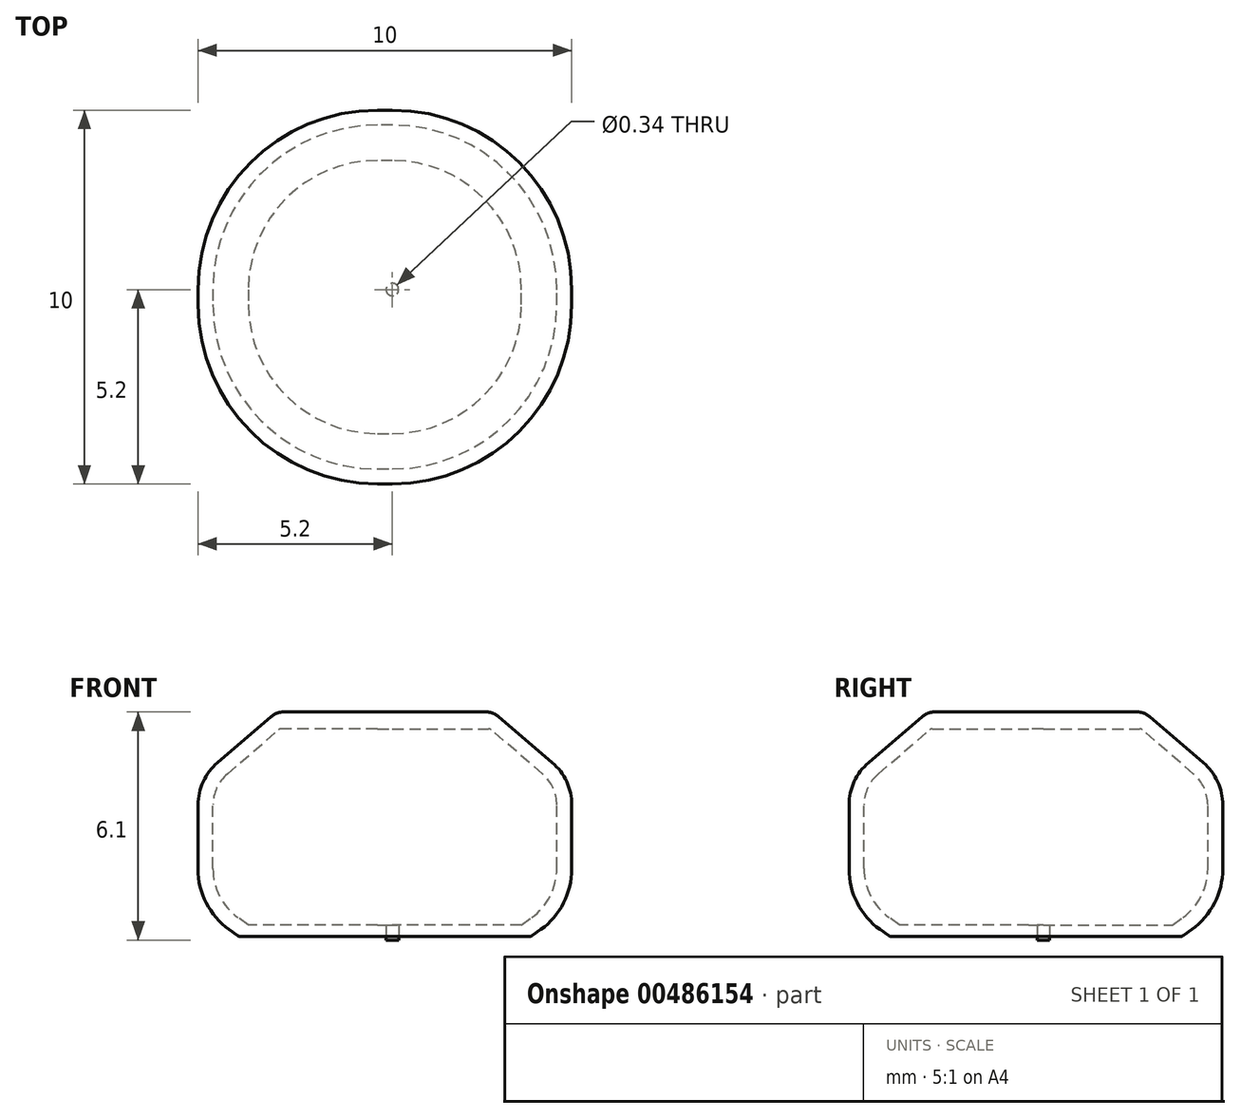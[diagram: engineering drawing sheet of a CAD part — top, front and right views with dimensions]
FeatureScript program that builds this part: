
annotation { "Feature Type Name" : "Feature", "Feature Type Description" : "" }
export const myFeature = defineFeature(function(context is Context, id is Id, definition is map)
    precondition{}
    {
        {
            assignVariable(context, id + "F0", {"name" : "l2", "anyValue" : 0.4});
        }
        {
            assignVariable(context, id + "F1", {"name" : "Scaf", "anyValue" : 0.65});
        }
        {
            var Q0;
            Q0=qCreatedBy(makeId("Front.planeOp"),FACE);
            var sketch = newSketch(context, id + "F2", { "sketchPlane" : qUnion([Q0])});
            skLineSegment(sketch, "E0", {"start": v(0, 0) * mm, "end": v(3.69, 0) * mm});
            skLineSegment(sketch, "E1", {"start": v(4.8, 1.8) * mm, "end": v(4.8, 3.51) * mm});
            skLineSegment(sketch, "E2", {"start": v(2.52, 6) * mm, "end": v(0, 6) * mm});
            skLineSegment(sketch, "E3", {"start": v(3.75, 0.02) * mm, "end": v(3.97, 0.18) * mm});
            skLineSegment(sketch, "E4", {"start": v(4.28, 4.65) * mm, "end": v(2.84, 5.88) * mm});
            skLineSegment(sketch, "E5", {"start": v(0, 0) * mm, "end": v(0, 0.3) * mm});
            skLineSegment(sketch, "E6", {"start": v(0, 0.3) * mm, "end": v(3.45, 0.3) * mm});
            skLineSegment(sketch, "E7", {"start": v(4.4, 1.81) * mm, "end": v(4.4, 3.51) * mm});
            skLineSegment(sketch, "E8", {"start": v(4.02, 4.35) * mm, "end": v(2.64, 5.53) * mm});
            skLineSegment(sketch, "E9", {"start": v(2.57, 5.55) * mm, "end": v(0, 5.55) * mm});
            skLineSegment(sketch, "E10", {"start": v(0, 5.55) * mm, "end": v(0, 6) * mm});
            skLineSegment(sketch, "E11", {"start": v(3.45, 0.3) * mm, "end": v(3.73, 0.5) * mm});
            skPoint(sketch, "E12.visualSharp", {"position": v(4.8, 0.78) * mm});
            skArc(sketch, "E12.filletArc", {"start": v(3.97, 0.18) * mm, "mid": v(4.58, 0.9) * mm, "end": v(4.8, 1.8) * mm});
            skPoint(sketch, "E13.visualSharp", {"position": v(4.8, 4.2) * mm});
            skArc(sketch, "E13.filletArc", {"start": v(4.8, 3.51) * mm, "mid": v(4.66, 4.14) * mm, "end": v(4.28, 4.65) * mm});
            skPoint(sketch, "E14.visualSharp", {"position": v(2.7, 6) * mm});
            skArc(sketch, "E14.filletArc", {"start": v(2.84, 5.88) * mm, "mid": v(2.69, 5.97) * mm, "end": v(2.52, 6) * mm});
            skPoint(sketch, "E15.visualSharp", {"position": v(2.61, 5.55) * mm});
            skArc(sketch, "E15.filletArc", {"start": v(2.64, 5.53) * mm, "mid": v(2.6, 5.54) * mm, "end": v(2.57, 5.55) * mm});
            skPoint(sketch, "E16.visualSharp", {"position": v(4.4, 4.02) * mm});
            skArc(sketch, "E16.filletArc", {"start": v(4.4, 3.51) * mm, "mid": v(4.3, 3.97) * mm, "end": v(4.02, 4.35) * mm});
            skPoint(sketch, "E17.visualSharp", {"position": v(4.4, 0.98) * mm});
            skArc(sketch, "E17.filletArc", {"start": v(3.73, 0.5) * mm, "mid": v(4.22, 1.08) * mm, "end": v(4.4, 1.81) * mm});
            skPoint(sketch, "E18.visualSharp", {"position": v(3.72, 0) * mm});
            skArc(sketch, "E18.filletArc", {"start": v(3.69, 0) * mm, "mid": v(3.72, 0) * mm, "end": v(3.75, 0.02) * mm});
            skSolve(sketch);
        }
        {
            var Q0;
            Q0=makeQuery(id+"F2.imprint","IMPRINT",FACE,{"disambiguationData":[TD([[makeQuery(id+"F2.imprint","IMPRINT",EDGE,{"derivedFrom":sQuery(id+"F2.wireOp",EDGE,"E0")}),1.0]])]});
            extrude(context, id + "F3", {"entities" : qUnion([Q0]), "depth" : (getVariable(context, 'l2')) * mm, "offsetDistance" : 25 * mm});
        }
        {
            var Q0;
            Q0=makeQuery(id+"F3.opExtrude","SWEPT_FACE",FACE,{"disambiguationData":[OSD([sQuery(id+"F2.wireOp",EDGE,"E10")])]});
            var Q1;
            Q1=sQuery(id+"F6.wireOp",EDGE,"E19");
            extrude(context, id + "F4", {"entities" : qUnion([Q0]), "operationType" : NewBodyOperationType.ADD, "surfaceEntities" : qUnion([Q1]), "depth" : (getVariable(context, 'Scaf')) * mm, "offsetDistance" : 25 * mm});
        }
        {
            var Q0;
            Q0=makeQuery(id+"F2.imprint","IMPRINT",FACE,{"disambiguationData":[TD([[makeQuery(id+"F2.imprint","IMPRINT",EDGE,{"derivedFrom":sQuery(id+"F2.wireOp",EDGE,"E0")}),1.0]])]});
            var Q1;
            Q1=sQuery(id+"F2.wireOp",EDGE,"E10");
            revolve(context, id + "F5", {"operationType" : NewBodyOperationType.ADD, "entities" : qUnion([Q0]), "axis" : qUnion([Q1]), "revolveType" : RevolveType.ONE_DIRECTION, "angle" : 90 * degree});
        }
        {
            var Q0;
            Q0=qCreatedBy(makeId("Front.planeOp"),FACE);
            var sketch = newSketch(context, id + "F6", { "sketchPlane" : qUnion([Q0])});
            skLineSegment(sketch, "E19", {"start": v(0, 0) * mm, "end": v(-0.4, 0) * mm});
            skLineSegment(sketch, "E20", {"start": v(-0.4, 0) * mm, "end": v(-0.4, 0.13) * mm});
            skSolve(sketch);
        }
        {
            var Q0;
            Q0=qCreatedBy(makeId("Front.planeOp"),FACE);
            cPlane(context, id + "F7", {"entities" : qUnion([Q0]), "cplaneType" : CPlaneType.OFFSET, "offset" : (getVariable(context, 'l2') / 2) * mm, "width" : 150 * mm, "height" : 150 * mm});
        }
        {
            var Q0;
            Q0=qCreatedBy(id+"F7.planeOp",FACE);
            var sketch = newSketch(context, id + "F8", { "sketchPlane" : qUnion([Q0])});
            skLineSegment(sketch, "E21", {"start": v(0, 0.03) * mm, "end": v(-0.2, 0.03) * mm});
            skLineSegment(sketch, "E22", {"start": v(-0.2, 0.03) * mm, "end": v(-0.2, 0.22) * mm});
            skLineSegment(sketch, "E23", {"start": v(0, 0.03) * mm, "end": v(0, 0.08) * mm});
            skLineSegment(sketch, "E24", {"start": v(0, 0.03) * mm, "end": v(0, 0.14) * mm});
            skPoint(sketch, "E24.endSnap0", {"position": v(0, 0.05) * mm});
            skSolve(sketch);
        }
        {
            var Q0;
            Q0=makeQuery(id+"F3.opExtrude","SWEPT_BODY",BODY,{"disambiguationData":[OSD([sQuery(id+"F2.wireOp",EDGE,"E0"),sQuery(id+"F2.wireOp",EDGE,"E1"),sQuery(id+"F2.wireOp",EDGE,"E2"),sQuery(id+"F2.wireOp",EDGE,"E3"),sQuery(id+"F2.wireOp",EDGE,"E4"),sQuery(id+"F2.wireOp",EDGE,"E5"),sQuery(id+"F2.wireOp",EDGE,"E6"),sQuery(id+"F2.wireOp",EDGE,"E7"),sQuery(id+"F2.wireOp",EDGE,"E8"),sQuery(id+"F2.wireOp",EDGE,"E9"),sQuery(id+"F2.wireOp",EDGE,"E10"),sQuery(id+"F2.wireOp",EDGE,"E11"),sQuery(id+"F2.wireOp",EDGE,"E12.filletArc"),sQuery(id+"F2.wireOp",EDGE,"E13.filletArc"),sQuery(id+"F2.wireOp",EDGE,"E14.filletArc"),sQuery(id+"F2.wireOp",EDGE,"E15.filletArc"),sQuery(id+"F2.wireOp",EDGE,"E16.filletArc"),sQuery(id+"F2.wireOp",EDGE,"E17.filletArc"),sQuery(id+"F2.wireOp",EDGE,"E18.filletArc")])]});
            var Q1;
            Q1=sQuery(id+"F8.wireOp",EDGE,"E22");
            transform(context, id + "F9", {"entities" : qUnion([Q0]), "transformType" : TransformType.ROTATION, "transformAxis" : qUnion([Q1]), "angle" : 90 * degree, "oppositeDirection" : true, "makeCopy" : true});
        }
        {
            var Q0;
            Q0=makeQuery(id+"F3.opExtrude","SWEPT_BODY",BODY,{"disambiguationData":[OSD([sQuery(id+"F2.wireOp",EDGE,"E0"),sQuery(id+"F2.wireOp",EDGE,"E1"),sQuery(id+"F2.wireOp",EDGE,"E2"),sQuery(id+"F2.wireOp",EDGE,"E3"),sQuery(id+"F2.wireOp",EDGE,"E4"),sQuery(id+"F2.wireOp",EDGE,"E5"),sQuery(id+"F2.wireOp",EDGE,"E6"),sQuery(id+"F2.wireOp",EDGE,"E7"),sQuery(id+"F2.wireOp",EDGE,"E8"),sQuery(id+"F2.wireOp",EDGE,"E9"),sQuery(id+"F2.wireOp",EDGE,"E10"),sQuery(id+"F2.wireOp",EDGE,"E11"),sQuery(id+"F2.wireOp",EDGE,"E12.filletArc"),sQuery(id+"F2.wireOp",EDGE,"E13.filletArc"),sQuery(id+"F2.wireOp",EDGE,"E14.filletArc"),sQuery(id+"F2.wireOp",EDGE,"E15.filletArc"),sQuery(id+"F2.wireOp",EDGE,"E16.filletArc"),sQuery(id+"F2.wireOp",EDGE,"E17.filletArc"),sQuery(id+"F2.wireOp",EDGE,"E18.filletArc")])]});
            var Q1;
            Q1=makeQuery(id+"F9.opPattern","COPY",BODY,{"derivedFrom":makeQuery(id+"F3.opExtrude","SWEPT_BODY",BODY,{"disambiguationData":[OSD([sQuery(id+"F2.wireOp",EDGE,"E0"),sQuery(id+"F2.wireOp",EDGE,"E1"),sQuery(id+"F2.wireOp",EDGE,"E2"),sQuery(id+"F2.wireOp",EDGE,"E3"),sQuery(id+"F2.wireOp",EDGE,"E4"),sQuery(id+"F2.wireOp",EDGE,"E5"),sQuery(id+"F2.wireOp",EDGE,"E6"),sQuery(id+"F2.wireOp",EDGE,"E7"),sQuery(id+"F2.wireOp",EDGE,"E8"),sQuery(id+"F2.wireOp",EDGE,"E9"),sQuery(id+"F2.wireOp",EDGE,"E10"),sQuery(id+"F2.wireOp",EDGE,"E11"),sQuery(id+"F2.wireOp",EDGE,"E12.filletArc"),sQuery(id+"F2.wireOp",EDGE,"E13.filletArc"),sQuery(id+"F2.wireOp",EDGE,"E14.filletArc"),sQuery(id+"F2.wireOp",EDGE,"E15.filletArc"),sQuery(id+"F2.wireOp",EDGE,"E16.filletArc"),sQuery(id+"F2.wireOp",EDGE,"E17.filletArc"),sQuery(id+"F2.wireOp",EDGE,"E18.filletArc")])]}),"instanceName":"1"});
            booleanBodies(context, id + "F10", {"operationType" : BooleanOperationType.UNION, "tools" : qUnion([Q0, Q1])});
        }
        {
            var Q0;
            Q0=makeQuery(id+"F3.opExtrude","SWEPT_BODY",BODY,{"disambiguationData":[OSD([sQuery(id+"F2.wireOp",EDGE,"E0"),sQuery(id+"F2.wireOp",EDGE,"E1"),sQuery(id+"F2.wireOp",EDGE,"E2"),sQuery(id+"F2.wireOp",EDGE,"E3"),sQuery(id+"F2.wireOp",EDGE,"E4"),sQuery(id+"F2.wireOp",EDGE,"E5"),sQuery(id+"F2.wireOp",EDGE,"E6"),sQuery(id+"F2.wireOp",EDGE,"E7"),sQuery(id+"F2.wireOp",EDGE,"E8"),sQuery(id+"F2.wireOp",EDGE,"E9"),sQuery(id+"F2.wireOp",EDGE,"E10"),sQuery(id+"F2.wireOp",EDGE,"E11"),sQuery(id+"F2.wireOp",EDGE,"E12.filletArc"),sQuery(id+"F2.wireOp",EDGE,"E13.filletArc"),sQuery(id+"F2.wireOp",EDGE,"E14.filletArc"),sQuery(id+"F2.wireOp",EDGE,"E15.filletArc"),sQuery(id+"F2.wireOp",EDGE,"E16.filletArc"),sQuery(id+"F2.wireOp",EDGE,"E17.filletArc"),sQuery(id+"F2.wireOp",EDGE,"E18.filletArc")])]});
            var Q1;
            Q1=sQuery(id+"F8.wireOp",EDGE,"E22");
            transform(context, id + "F11", {"entities" : qUnion([Q0]), "transformType" : TransformType.ROTATION, "transformAxis" : qUnion([Q1]), "angle" : 180 * degree, "makeCopy" : true});
        }
        {
            var Q0;
            Q0=makeQuery(id+"F3.opExtrude","SWEPT_BODY",BODY,{"disambiguationData":[OSD([sQuery(id+"F2.wireOp",EDGE,"E0"),sQuery(id+"F2.wireOp",EDGE,"E1"),sQuery(id+"F2.wireOp",EDGE,"E2"),sQuery(id+"F2.wireOp",EDGE,"E3"),sQuery(id+"F2.wireOp",EDGE,"E4"),sQuery(id+"F2.wireOp",EDGE,"E5"),sQuery(id+"F2.wireOp",EDGE,"E6"),sQuery(id+"F2.wireOp",EDGE,"E7"),sQuery(id+"F2.wireOp",EDGE,"E8"),sQuery(id+"F2.wireOp",EDGE,"E9"),sQuery(id+"F2.wireOp",EDGE,"E10"),sQuery(id+"F2.wireOp",EDGE,"E11"),sQuery(id+"F2.wireOp",EDGE,"E12.filletArc"),sQuery(id+"F2.wireOp",EDGE,"E13.filletArc"),sQuery(id+"F2.wireOp",EDGE,"E14.filletArc"),sQuery(id+"F2.wireOp",EDGE,"E15.filletArc"),sQuery(id+"F2.wireOp",EDGE,"E16.filletArc"),sQuery(id+"F2.wireOp",EDGE,"E17.filletArc"),sQuery(id+"F2.wireOp",EDGE,"E18.filletArc")])]});
            var Q1;
            Q1=makeQuery(id+"F11.opPattern","COPY",BODY,{"derivedFrom":makeQuery(id+"F3.opExtrude","SWEPT_BODY",BODY,{"disambiguationData":[OSD([sQuery(id+"F2.wireOp",EDGE,"E0"),sQuery(id+"F2.wireOp",EDGE,"E1"),sQuery(id+"F2.wireOp",EDGE,"E2"),sQuery(id+"F2.wireOp",EDGE,"E3"),sQuery(id+"F2.wireOp",EDGE,"E4"),sQuery(id+"F2.wireOp",EDGE,"E5"),sQuery(id+"F2.wireOp",EDGE,"E6"),sQuery(id+"F2.wireOp",EDGE,"E7"),sQuery(id+"F2.wireOp",EDGE,"E8"),sQuery(id+"F2.wireOp",EDGE,"E9"),sQuery(id+"F2.wireOp",EDGE,"E10"),sQuery(id+"F2.wireOp",EDGE,"E11"),sQuery(id+"F2.wireOp",EDGE,"E12.filletArc"),sQuery(id+"F2.wireOp",EDGE,"E13.filletArc"),sQuery(id+"F2.wireOp",EDGE,"E14.filletArc"),sQuery(id+"F2.wireOp",EDGE,"E15.filletArc"),sQuery(id+"F2.wireOp",EDGE,"E16.filletArc"),sQuery(id+"F2.wireOp",EDGE,"E17.filletArc"),sQuery(id+"F2.wireOp",EDGE,"E18.filletArc")])]}),"instanceName":"1"});
            booleanBodies(context, id + "F12", {"operationType" : BooleanOperationType.UNION, "tools" : qUnion([Q0, Q1])});
        }
        {
            var Q0;
            {var subQ0=sQuery(id+"F2.wireOp",EDGE,"E18.filletArc");var subQ1=sQuery(id+"F2.wireOp",EDGE,"E17.filletArc");var subQ2=sQuery(id+"F2.wireOp",EDGE,"E16.filletArc");var subQ3=sQuery(id+"F2.wireOp",EDGE,"E15.filletArc");var subQ4=sQuery(id+"F2.wireOp",EDGE,"E14.filletArc");var subQ5=sQuery(id+"F2.wireOp",EDGE,"E13.filletArc");var subQ6=sQuery(id+"F2.wireOp",EDGE,"E12.filletArc");var subQ7=sQuery(id+"F2.wireOp",EDGE,"E11");var subQ8=sQuery(id+"F2.wireOp",EDGE,"E10");var subQ9=sQuery(id+"F2.wireOp",EDGE,"E9");var subQ10=sQuery(id+"F2.wireOp",EDGE,"E8");var subQ11=sQuery(id+"F2.wireOp",EDGE,"E7");var subQ12=sQuery(id+"F2.wireOp",EDGE,"E6");var subQ13=sQuery(id+"F2.wireOp",EDGE,"E5");var subQ14=sQuery(id+"F2.wireOp",EDGE,"E4");var subQ15=sQuery(id+"F2.wireOp",EDGE,"E3");var subQ16=sQuery(id+"F2.wireOp",EDGE,"E2");var subQ17=sQuery(id+"F2.wireOp",EDGE,"E1");var subQ18=sQuery(id+"F2.wireOp",EDGE,"E0");var subQ19=makeQuery(id+"F5.opRevolve","CAP_FACE",FACE,{"disambiguationData":[OSD([subQ18,subQ17,subQ16,subQ15,subQ14,subQ13,subQ12,subQ11,subQ10,subQ9,subQ8,subQ7,subQ6,subQ5,subQ4,subQ3,subQ2,subQ1,subQ0])],"isStart":false});var subQ32=makeQuery(id+"F3.opExtrude","SWEPT_FACE",FACE,{"disambiguationData":[OSD([subQ13])]});var subQ33=makeQuery(id+"F3.opExtrude","SWEPT_FACE",FACE,{"disambiguationData":[OSD([subQ8])]});var subQ35=makeQuery(id+"F3.opExtrude","SWEPT_FACE",FACE,{"disambiguationData":[OSD([subQ16])]});Q0=makeQuery(id+"F11.opPattern","COPY",FACE,{"derivedFrom":makeQuery(id+"F10.opBoolean","SPLIT",FACE,{"disambiguationData":[TD([subQ35])],"derivedFrom":makeQuery(id+"F9.opPattern","COPY",FACE,{"derivedFrom":makeQuery(id+"F5.boolean.opBoolean","MERGE",FACE,{"derivedFrom":[subQ32,subQ33,subQ19]}),"instanceName":"1"})}),"instanceName":"1"});}
            extrude(context, id + "F13", {"entities" : qUnion([Q0]), "operationType" : NewBodyOperationType.ADD, "depth" : (getVariable(context, 'l2') * 1.5) * mm, "offsetDistance" : 25 * mm});
        }
        {
            var Q0;
            {var subQ0=sQuery(id+"F2.wireOp",EDGE,"E0");var subQ1=makeQuery(id+"F5.boolean.opBoolean","MERGE",FACE,{"derivedFrom":[makeQuery(id+"F3.opExtrude","SWEPT_FACE",FACE,{"disambiguationData":[OSD([subQ0])]}),makeQuery(id+"F5.opRevolve","SWEPT_FACE",FACE,{"disambiguationData":[OSD([subQ0])]})]});var subQ2=makeQuery(id+"F10.opBoolean","MERGE",FACE,{"derivedFrom":[subQ1,makeQuery(id+"F9.opPattern","COPY",FACE,{"derivedFrom":subQ1,"instanceName":"1"})]});Q0=makeQuery(id+"F13.boolean.opBoolean","MERGE",FACE,{"derivedFrom":[makeQuery(id+"F12.opBoolean","MERGE",FACE,{"derivedFrom":[subQ2,makeQuery(id+"F11.opPattern","COPY",FACE,{"derivedFrom":subQ2,"instanceName":"1"})]}),makeQuery(id+"F13.opExtrude","SWEPT_FACE",FACE,{"disambiguationData":[OSD([subQ0,sQuery(id+"F2.wireOp",EDGE,"E5")])]})]});}
            var sketch = newSketch(context, id + "F14", { "sketchPlane" : qUnion([Q0])});
            skCircle(sketch, "E25", {"center": v(0, 0) * mm, "radius": 0.17 * mm});
            skSolve(sketch);
        }
        {
            var Q0;
            Q0=makeQuery(id+"F14.imprint","IMPRINT",FACE,{"disambiguationData":[TD([[makeQuery(id+"F14.imprint","IMPRINT",EDGE,{"derivedFrom":sQuery(id+"F14.wireOp",EDGE,"E25")}),-1.0]])]});
            cPlane(context, id + "F15", {"entities" : qUnion([Q0]), "cplaneType" : CPlaneType.OFFSET, "offset" : .1 * mm, "width" : 150 * mm, "height" : 150 * mm});
        }
        {
            var Q0;
            Q0=qCreatedBy(id+"F15.planeOp",FACE);
            var sketch = newSketch(context, id + "F16", { "sketchPlane" : qUnion([Q0])});
            skLineSegment(sketch, "E26", {"start": v(0, 0) * mm, "end": v(-0.33, -0.11) * mm});
            skSolve(sketch);
        }
        {
            var Q0;
            Q0=makeQuery(id+"F14.imprint","IMPRINT",FACE,{"disambiguationData":[TD([[makeQuery(id+"F14.imprint","IMPRINT",EDGE,{"derivedFrom":sQuery(id+"F14.wireOp",EDGE,"E25")}),1.0]])]});
            extrude(context, id + "F17", {"entities" : qUnion([Q0]), "operationType" : NewBodyOperationType.ADD, "depth" : .1 * mm, "offsetDistance" : 25 * mm});
        }
        {
            var Q1;
            Q1=makeQuery(id+"F14.imprint","IMPRINT",FACE,{"disambiguationData":[TD([[makeQuery(id+"F14.imprint","IMPRINT",EDGE,{"derivedFrom":sQuery(id+"F14.wireOp",EDGE,"E25")}),1.0]])]});
            var Q2;
            Q2=sQuery(id+"F16.wireOp",VERTEX,"E26.start");
            loft(context, id + "F18", {"operationType" : NewBodyOperationType.ADD, "sheetProfilesArray" : [{ "sheetProfileEntities" : qUnion([Q1]) }, { "sheetProfileEntities" : qUnion([Q2]) }]});
        }
        {
            var Q0;
            Q0=makeQuery(id+"F14.imprint","IMPRINT",FACE,{"disambiguationData":[TD([[makeQuery(id+"F14.imprint","IMPRINT",EDGE,{"derivedFrom":sQuery(id+"F14.wireOp",EDGE,"E25")}),1.0]])]});
            extrude(context, id + "F19", {"entities" : qUnion([Q0]), "operationType" : NewBodyOperationType.REMOVE, "oppositeDirection" : true, "depth" : 1 * mm, "offsetDistance" : 25 * mm});
        }
    });
